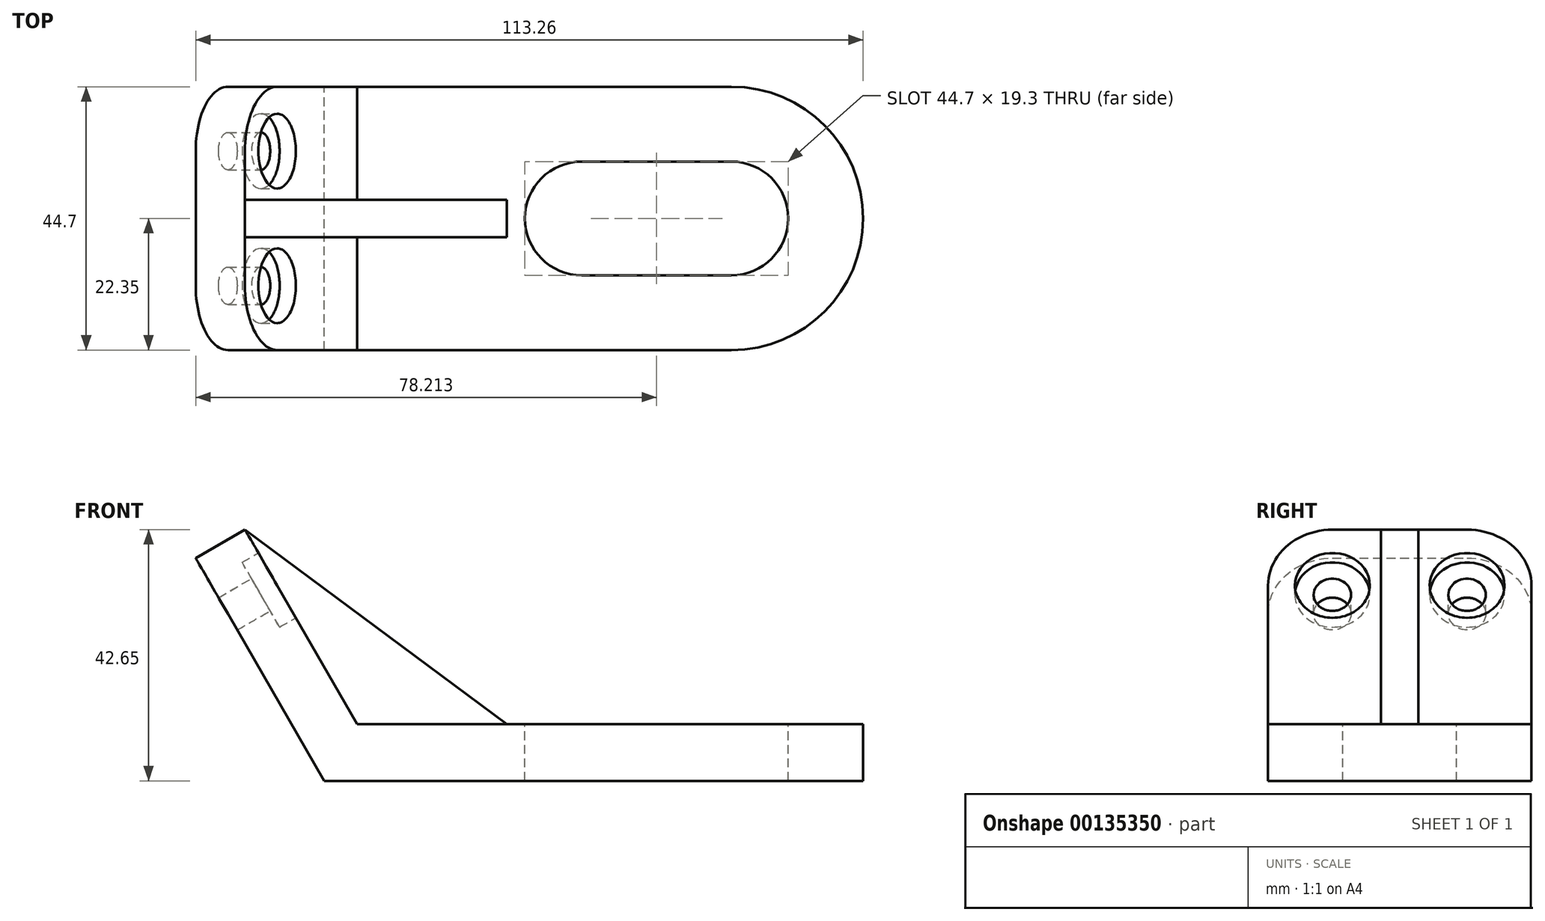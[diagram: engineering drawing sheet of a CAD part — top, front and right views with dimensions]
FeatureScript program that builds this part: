
annotation { "Feature Type Name" : "Feature", "Feature Type Description" : "" }
export const myFeature = defineFeature(function(context is Context, id is Id, definition is map)
    precondition{}
    {
        {
            var Q0;
            Q0=qCreatedBy(makeId("Front.planeOp"),FACE);
            var sketch = newSketch(context, id + "F0", { "sketchPlane" : qUnion([Q0])});
            skLineSegment(sketch, "E0", {"start": v(0, 0) * mm, "end": v(91.42, 0) * mm});
            skLineSegment(sketch, "E1", {"start": v(91.42, 0) * mm, "end": v(91.42, 9.65) * mm});
            skLineSegment(sketch, "E2", {"start": v(0, 0) * mm, "end": v(-21.84, 37.82) * mm});
            skLineSegment(sketch, "E3", {"start": v(-21.84, 37.82) * mm, "end": v(-13.48, 42.65) * mm});
            skLineSegment(sketch, "E4", {"start": v(-13.48, 42.65) * mm, "end": v(5.57, 9.65) * mm});
            skLineSegment(sketch, "E5", {"start": v(5.57, 9.65) * mm, "end": v(91.42, 9.65) * mm});
            skSolve(sketch);
        }
        {
            var Q0;
            Q0 = qSketchRegion(id + "F0", true);
            extrude(context, id + "F1", {"entities" : qUnion([Q0]), "depth" : 22.35 * mm, "hasSecondDirection" : true, "secondDirectionOppositeDirection" : true, "secondDirectionDepth" : 22.35 * mm});
        }
        {
            var Q0;
            Q0=qCreatedBy(makeId("Front.planeOp"),FACE);
            var sketch = newSketch(context, id + "F2", { "sketchPlane" : qUnion([Q0])});
            skLineSegment(sketch, "E6.0", {"start": v(5.57, 9.65) * mm, "end": v(91.42, 9.65) * mm, "construction": true});
            skLineSegment(sketch, "E7.0", {"start": v(-13.48, 42.65) * mm, "end": v(5.57, 9.65) * mm, "construction": true});
            skPoint(sketch, "E8", {"position": v(30.97, 9.65) * mm});
            skLineSegment(sketch, "E9", {"start": v(-13.48, 42.65) * mm, "end": v(30.97, 9.65) * mm});
            skLineSegment(sketch, "E10", {"start": v(-13.48, 42.65) * mm, "end": v(5.57, 9.65) * mm});
            skLineSegment(sketch, "E11", {"start": v(5.57, 9.65) * mm, "end": v(30.97, 9.65) * mm});
            skSolve(sketch);
        }
        {
            var Q0;
            Q0 = qSketchRegion(id + "F2", true);
            extrude(context, id + "F3", {"entities" : qUnion([Q0]), "operationType" : NewBodyOperationType.ADD, "depth" : 3.17 * mm, "hasSecondDirection" : true, "secondDirectionOppositeDirection" : true, "secondDirectionDepth" : 3.17 * mm});
        }
        {
            var Q0;
            Q0=makeQuery(id+"F1.opExtrude","CAP_EDGE",EDGE,{"disambiguationData":[OSD([sQuery(id+"F0.wireOp",EDGE,"E3")])],"isStart":false});
            var Q1;
            Q1=makeQuery(id+"F1.opExtrude","CAP_EDGE",EDGE,{"disambiguationData":[OSD([sQuery(id+"F0.wireOp",EDGE,"E3")])],"isStart":true});
            fillet(context, id + "F4", {"entities" : qUnion([Q0, Q1]), "radius" : 10.92 * mm, "tangentPropagation" : true, "allowEdgeOverflow" : false});
        }
        {
            var Q0;
            Q0=makeQuery(id+"F1.opExtrude","CAP_EDGE",EDGE,{"disambiguationData":[OSD([sQuery(id+"F0.wireOp",EDGE,"E1")])],"isStart":false});
            var Q1;
            Q1=makeQuery(id+"F1.opExtrude","CAP_EDGE",EDGE,{"disambiguationData":[OSD([sQuery(id+"F0.wireOp",EDGE,"E1")])],"isStart":true});
            fillet(context, id + "F5", {"entities" : qUnion([Q0, Q1]), "radius" : 22.35 * mm, "tangentPropagation" : true, "allowEdgeOverflow" : false});
        }
        {
            var Q0;
            Q0=makeQuery(id+"F1.opExtrude","SWEPT_FACE",FACE,{"disambiguationData":[OSD([sQuery(id+"F0.wireOp",EDGE,"E5")])]});
            var sketch = newSketch(context, id + "F6", { "sketchPlane" : qUnion([Q0])});
            skLineSegment(sketch, "E12.0", {"start": v(5.57, -22.35) * mm, "end": v(5.57, -3.18) * mm});
            skPoint(sketch, "E13", {"position": v(43.67, 0) * mm});
            skPoint(sketch, "E14", {"position": v(69.07, 0) * mm});
            skArc(sketch, "E15", {"start": v(69.07, -9.65) * mm, "mid": v(78.72, 0) * mm, "end": v(69.07, 9.65) * mm});
            skArc(sketch, "E16", {"start": v(43.67, 9.65) * mm, "mid": v(34.02, 0) * mm, "end": v(43.67, -9.65) * mm});
            skLineSegment(sketch, "E17", {"start": v(43.67, 9.65) * mm, "end": v(69.07, 9.65) * mm});
            skLineSegment(sketch, "E18", {"start": v(43.67, -9.65) * mm, "end": v(69.07, -9.65) * mm});
            skArc(sketch, "E19.0", {"start": v(69.07, -22.35) * mm, "mid": v(91.42, 0) * mm, "end": v(69.07, 22.35) * mm});
            skSolve(sketch);
        }
        {
            var Q0;
            Q0 = qSketchRegion(id + "F6", true);
            var Q1;
            Q1=makeQuery(id+"F1.opExtrude","SWEPT_FACE",FACE,{"disambiguationData":[OSD([sQuery(id+"F0.wireOp",EDGE,"E0")])]});
            extrude(context, id + "F7", {"entities" : qUnion([Q0]), "operationType" : NewBodyOperationType.REMOVE, "endBound" : BoundingType.UP_TO_SURFACE, "oppositeDirection" : true, "endBoundEntityFace" : qUnion([Q1]), "depth" : 25.4 * mm});
        }
        {
            var Q0;
            {var subQ0=sQuery(id+"F2.wireOp",EDGE,"E9");var subQ3=sQuery(id+"F0.wireOp",EDGE,"E4");Q0=makeQuery(id+"F3.boolean.opBoolean","SPLIT",FACE,{"disambiguationData":[TD([makeQuery(id+"F3.opExtrude","CAP_FACE",FACE,{"disambiguationData":[OSD([subQ0,sQuery(id+"F2.wireOp",EDGE,"E10"),sQuery(id+"F2.wireOp",EDGE,"E11")])],"isStart":false})])],"derivedFrom":makeQuery(id+"F1.opExtrude","SWEPT_FACE",FACE,{"disambiguationData":[OSD([subQ3])]})});}
            var sketch = newSketch(context, id + "F8", { "sketchPlane" : qUnion([Q0])});
            skLineSegment(sketch, "E20.0", {"start": v(-11.43, 43.67) * mm, "end": v(-3.18, 43.67) * mm});
            skLineSegment(sketch, "E21.0", {"start": v(-22.35, 5.57) * mm, "end": v(-3.18, 5.57) * mm});
            skSolve(sketch);
        }
        {
            var Q0;
            Q0=makeQuery(id+"F8.imprint","IMPRINT",FACE,{"disambiguationData":[TD([[makeQuery(id+"F8.imprint","IMPRINT",EDGE,{"derivedFrom":sQuery(id+"F8.wireOp",EDGE,"E20.0")}),-1.0]])]});
            var sketch = newSketch(context, id + "F9", { "sketchPlane" : qUnion([Q0])});
            skLineSegment(sketch, "E22.0", {"start": v(-11.43, 43.67) * mm, "end": v(-3.18, 43.67) * mm, "construction": true});
            skLineSegment(sketch, "E23.0", {"start": v(-22.35, 5.57) * mm, "end": v(-3.18, 5.57) * mm});
            skArc(sketch, "E24.0", {"start": v(-11.43, 43.67) * mm, "mid": v(-19.15, 40.47) * mm, "end": v(-22.35, 32.75) * mm, "construction": true});
            skCircle(sketch, "E25", {"center": v(-11.43, 32.75) * mm, "radius": 3.18 * mm});
            skCircle(sketch, "E26", {"center": v(-11.43, 32.75) * mm, "radius": 6.35 * mm});
            skSolve(sketch);
        }
        {
            var Q0;
            Q0=makeQuery(id+"F9.imprint","IMPRINT",FACE,{"disambiguationData":[TD([[makeQuery(id+"F9.imprint","IMPRINT",EDGE,{"derivedFrom":sQuery(id+"F9.wireOp",EDGE,"E25")}),-1.0]])]});
            var Q1;
            Q1=makeQuery(id+"F9.imprint","IMPRINT",FACE,{"disambiguationData":[TD([[makeQuery(id+"F9.imprint","IMPRINT",EDGE,{"derivedFrom":sQuery(id+"F9.wireOp",EDGE,"E25")}),1.0]])]});
            extrude(context, id + "F10", {"entities" : qUnion([Q0, Q1]), "operationType" : NewBodyOperationType.REMOVE, "oppositeDirection" : true, "depth" : 3.17 * mm});
        }
        {
            var Q0;
            Q0=makeQuery(id+"F9.imprint","IMPRINT",FACE,{"disambiguationData":[TD([[makeQuery(id+"F9.imprint","IMPRINT",EDGE,{"derivedFrom":sQuery(id+"F9.wireOp",EDGE,"E25")}),1.0]])]});
            extrude(context, id + "F11", {"entities" : qUnion([Q0]), "operationType" : NewBodyOperationType.REMOVE, "endBound" : BoundingType.THROUGH_ALL, "oppositeDirection" : true, "depth" : 25.4 * mm});
        }
        {
            var Q0;
            {var subQ2=sQuery(id+"F2.wireOp",EDGE,"E9");var subQ3=sQuery(id+"F0.wireOp",EDGE,"E4");Q0=makeQuery(id+"F3.boolean.opBoolean","SPLIT",FACE,{"disambiguationData":[TD([makeQuery(id+"F3.opExtrude","CAP_FACE",FACE,{"disambiguationData":[OSD([subQ2,sQuery(id+"F2.wireOp",EDGE,"E10"),sQuery(id+"F2.wireOp",EDGE,"E11")])],"isStart":true})])],"derivedFrom":makeQuery(id+"F1.opExtrude","SWEPT_FACE",FACE,{"disambiguationData":[OSD([subQ3])]})});}
            var sketch = newSketch(context, id + "F12", { "sketchPlane" : qUnion([Q0])});
            skArc(sketch, "E27.0", {"start": v(22.35, 32.75) * mm, "mid": v(19.15, 40.47) * mm, "end": v(11.43, 43.67) * mm});
            skCircle(sketch, "E28", {"center": v(11.43, 32.75) * mm, "radius": 6.35 * mm});
            skCircle(sketch, "E29", {"center": v(11.43, 32.75) * mm, "radius": 3.18 * mm});
            skSolve(sketch);
        }
        {
            var Q0;
            Q0 = qSketchRegion(id + "F12", true);
            var Q1;
            Q1=makeQuery(id+"F12.imprint","IMPRINT",FACE,{"disambiguationData":[TD([[makeQuery(id+"F12.imprint","IMPRINT",EDGE,{"derivedFrom":sQuery(id+"F12.wireOp",EDGE,"E29")}),1.0]])]});
            extrude(context, id + "F13", {"entities" : qUnion([Q0, Q1]), "operationType" : NewBodyOperationType.REMOVE, "oppositeDirection" : true, "depth" : 3.19 * mm});
        }
        {
            var Q0;
            Q0=makeQuery(id+"F12.imprint","IMPRINT",FACE,{"disambiguationData":[TD([[makeQuery(id+"F12.imprint","IMPRINT",EDGE,{"derivedFrom":sQuery(id+"F12.wireOp",EDGE,"E29")}),1.0]])]});
            extrude(context, id + "F14", {"entities" : qUnion([Q0]), "operationType" : NewBodyOperationType.REMOVE, "endBound" : BoundingType.THROUGH_ALL, "oppositeDirection" : true, "depth" : 25.4 * mm});
        }
    });
